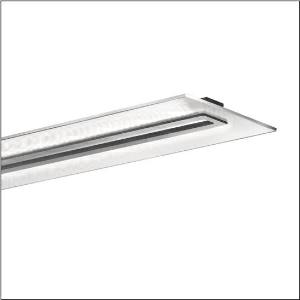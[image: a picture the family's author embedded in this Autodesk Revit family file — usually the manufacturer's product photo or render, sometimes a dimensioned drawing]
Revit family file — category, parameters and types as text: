
# Revit family: vega_r__11_5mn238dlc0s_c747
name_source: partatom
category: Lighting Fixtures
units: mm (PartAtom-declared; Revit-internal decimal feet)

## family parameters
Cut with Voids When Loaded = No
Host = Face
Light Source = No
Part Type = Normal
Room Calculation Point = No
Round Connector Dimension = Use Diameter
Shared = No

## types (1)
- --- (1 x LED 4000K / CRI = 80 (unbekannt), 4300 lm, 4000K)
    Apparent Load = 31 VA
    CIE Flux Codes = 61 86 97 62 100
    Color Rendering = 80
    Color Temperature = 4000K
    Default Elevation = 1800 mm
    Description = Vega® 11, office luminaire, primary light control with prismatic reflector, of PMMA, transparent prismatic structure, CAT 2 (L<= 1500cd/m²), light emission: direct/indirect distribution, primary light characteristic: symmetric, installation type: suspended mounting, surface-mounted, LED, rated luminous flux: 4.300lm, luminous efficacy: 139lm/W, light colour: 840, colour temperature: 4000K, control gear: ECG, with terminal, 3+2-pole, max. 2.5mm², mains connection: 230V, AC, 50Hz, connection cable inclusive, cable length: 1,5m, rated input power: 31W, luminaire housing, rectangular, rounded, of aluminium section, anodised, metallic grey (RAL 9006), length: 1.250mm, width: 350mm, height: 43mm, luminaire housing, lower part, of aluminium section, anodised, metallic grey (RAL 9006), of PC, grey, protection rating (complete): IP20, insulation class (complete): insulation class I (protective earthing), certification: CE, permissible operating ambient temperature: 0..+35°C, standard: EN 50419, packaging unit: 1 piece
    Height = 40 mm  [stored 0.131234 ft]
    Lamp = 1 x LED 4000K / CRI >= 80 (unbekannt)
    Lamp Light Flux = 4300 lm
    Lamp count = 1
    Length = 1250 mm
    Luminous efficacy = 139 lm/W
    Manufacturer = Siteco
    ModVariant = No
    Model = 5MN238DLC0S
    Mounting Place = Ceiling
    Mounting Type = Pendant
    Number of Poles = 1
    OnlyDefault = Yes
    Power Factor = 1
    Product Name = Vega® 11
    Product group = office luminaire | ceiling pendant
    ProductGroupID = 902
    Protection Class = Protection class I
    Protection Degree = IP 20
    RLX_Detail_Level = 1
    RLX_Emergency_Light_Flux = 0 lm
    RLX_Emergency_Type = 0
    RLX_Emergency_Type_DB = No
    RlxData = <blob elided: 62969 chars, md5=6979dfda>
    Socket = socket
    Standby Power = 0 W
    System Light Flux = 4300 lm
    System Power = 31 W
    Type Comments = factory setting: luminous flux: 100 % | dim-lin: 254 | 231 mA
    Type Image = l_1004807.jpg
    URL = http://relux.com
    VarID = @adj_165621
    Voltage = 0 V
    Weight = 0.00 kg
    Width = 350 mm

note: [stored X ft] marks values corroborated as IEEE doubles in the binary element streams (Revit-internal decimal feet)

## geometry (parser evidence)
native form markers: Blend x4, Sweep x11
no freeform markers — native parametric forms only
